# Revit family: NEST_Classic_round_VIZULO
name_source: partatom
category: Lighting Fixtures
units: mm (PartAtom-declared; Revit-internal decimal feet)

## family parameters
Always vertical = Yes
Cut with Voids When Loaded = No
Light Source = Yes
OmniClass Number = 23.80.70.00
OmniClass Title = Lighting
Part Type = Normal
Room Calculation Point = No
Round Connector Dimension = Use Diameter
Shared = No
Work Plane-Based = No

## types (20) — shared parameters
Color Filter = 16777215
Colour = Aluminium
Dimming Lamp Color Temperature Shift = <None>
Emit Shape Visible in Rendering = No
Emit from Circle Diameter = 160 mm  [stored 0.524934 ft]
Light Source Symbol Length = 3048 mm  [stored 10 ft]
Spot Beam Angle = 30.00°
Spot Field Angle = 90.00°
Tilt Angle = 90.00°
zero-valued in all types: Default Elevation

## type names (no varying parameters)
- 180 mm, 12 W, 3000 K
- 180 mm, 12 W, 4000 K
- 180 mm, 28 W, 3000 K
- 180 mm, 28 W, 4000 K
- 180 mm, 35 W, 3000 K
- 180 mm, 35 W, 4000 K
- 180 mm, 40 W, 3000 K
- 180 mm, 40 W, 4000 K
- 180 mm, 20 W, 3000 K
- 180 mm, 20 W, 4000 K
- 225 mm, 12 W, 3000 K
- 225 mm, 12 W, 4000 K
- 225 mm, 28 W, 3000 K
- 225 mm, 28 W, 4000 K
- 225 mm, 35 W, 3000 K
- 225 mm, 35 W, 4000 K
- 225 mm, 40 W, 3000 K
- 225 mm, 40 W, 4000 K
- 225 mm, 20 W, 3000 K
- 225 mm, 20 W, 4000 K

note: [stored X ft] marks values corroborated as IEEE doubles in the binary element streams (Revit-internal decimal feet)

## geometry (parser evidence)
native form markers: Sweep x2
no freeform markers — native parametric forms only
